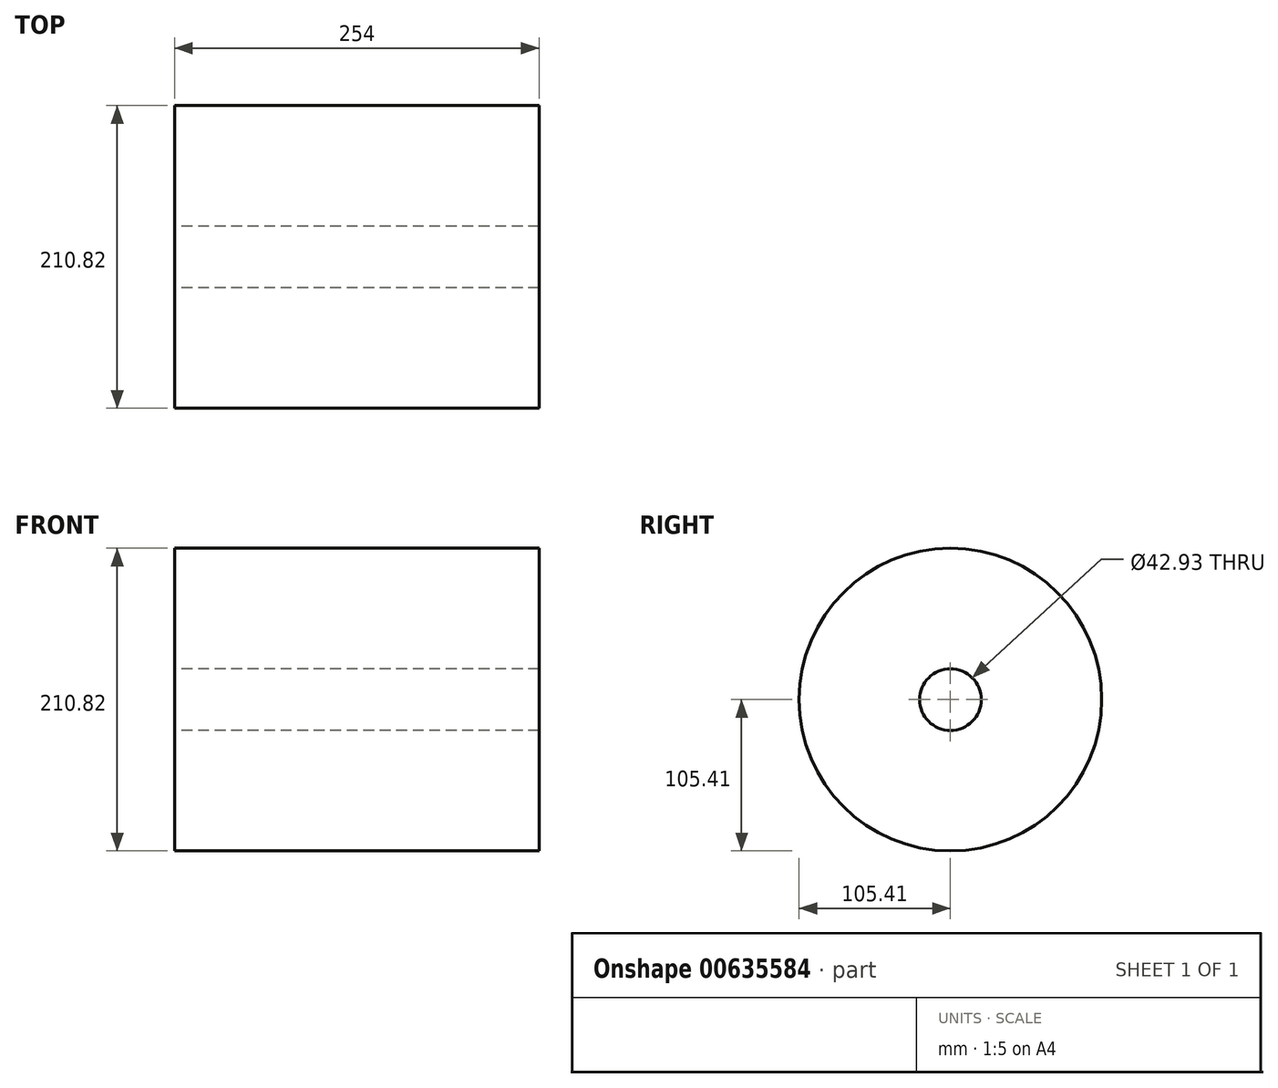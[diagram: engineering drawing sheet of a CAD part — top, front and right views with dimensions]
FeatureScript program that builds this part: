
annotation { "Feature Type Name" : "Feature", "Feature Type Description" : "" }
export const myFeature = defineFeature(function(context is Context, id is Id, definition is map)
    precondition{}
    {
        {
            var Q0;
            Q0=qCreatedBy(makeId("Right.planeOp"),FACE);
            var sketch = newSketch(context, id + "F0", { "sketchPlane" : qUnion([Q0])});
            skCircle(sketch, "E0", {"center": v(0, 0) * mm, "radius": 105.41 * mm});
            skSolve(sketch);
        }
        {
            var Q0;
            Q0 = qSketchRegion(id + "F0", true);
            extrude(context, id + "F1", {"entities" : qUnion([Q0]), "depth" : 127 * mm, "offsetDistance" : 25.4 * mm, "hasSecondDirection" : true, "secondDirectionOppositeDirection" : true, "secondDirectionDepth" : 127 * mm});
        }
        {
            var Q0;
            Q0=makeQuery(id+"F1.opExtrude","CAP_FACE",FACE,{"disambiguationData":[OSD([sQuery(id+"F0.wireOp",EDGE,"E0")])],"isStart":true});
            var sketch = newSketch(context, id + "F2", { "sketchPlane" : qUnion([Q0])});
            skCircle(sketch, "E1", {"center": v(0, 0) * mm, "radius": 21.46 * mm});
            skSolve(sketch);
        }
        {
            var Q0;
            Q0 = qSketchRegion(id + "F2", true);
            extrude(context, id + "F3", {"entities" : qUnion([Q0]), "operationType" : NewBodyOperationType.REMOVE, "oppositeDirection" : true, "depth" : 254 * mm, "offsetDistance" : 25.4 * mm});
        }
    });
